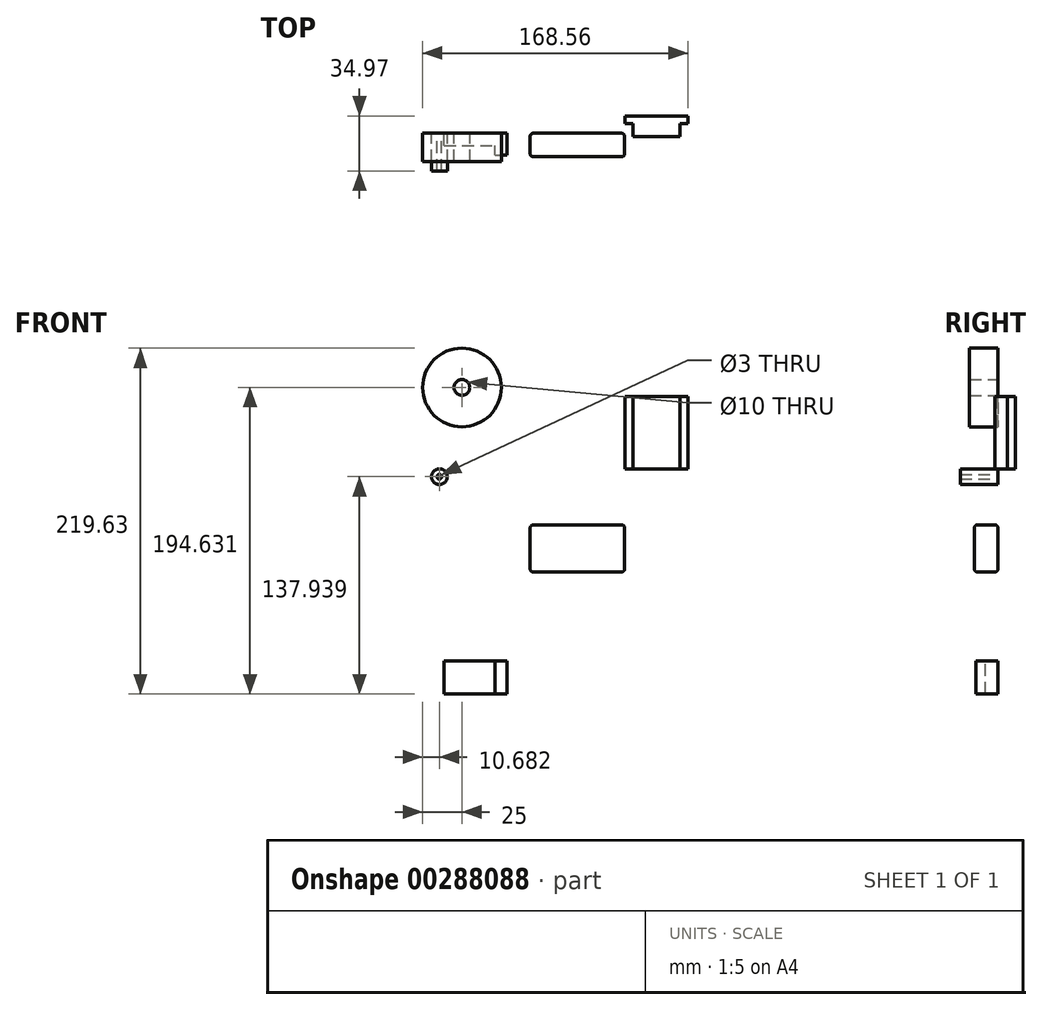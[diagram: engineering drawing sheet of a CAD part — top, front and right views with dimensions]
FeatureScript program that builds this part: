
annotation { "Feature Type Name" : "Feature", "Feature Type Description" : "" }
export const myFeature = defineFeature(function(context is Context, id is Id, definition is map)
    precondition{}
    {
        {
            var Q0;
            Q0=qCreatedBy(makeId("Front.planeOp"),FACE);
            var sketch = newSketch(context, id + "F0", { "sketchPlane" : qUnion([Q0])});
            skCircle(sketch, "E0", {"center": v(-49.92, 51.66) * mm, "radius": 25 * mm});
            skCircle(sketch, "E1", {"center": v(-49.92, 51.66) * mm, "radius": 5 * mm});
            skSolve(sketch);
        }
        {
            var Q0;
            Q0=makeQuery(id+"F0.imprint","IMPRINT",FACE,{"disambiguationData":[TD([[makeQuery(id+"F0.imprint","IMPRINT",EDGE,{"derivedFrom":sQuery(id+"F0.wireOp",EDGE,"E0")}),1.0]])]});
            extrude(context, id + "F1", {"entities" : qUnion([Q0]), "depth" : 18 * mm});
        }
        {
            var Q0;
            Q0=qCreatedBy(makeId("Front.planeOp"),FACE);
            var sketch = newSketch(context, id + "F2", { "sketchPlane" : qUnion([Q0])});
            skCircle(sketch, "E2", {"center": v(-64.24, -5.03) * mm, "radius": 5 * mm});
            skCircle(sketch, "E3", {"center": v(-64.24, -5.03) * mm, "radius": 1.5 * mm});
            skSolve(sketch);
        }
        {
            var Q0;
            Q0=qSketchRegion(id+"F2",true);
            extrude(context, id + "F3", {"entities" : qUnion([Q0]), "depth" : 24 * mm});
        }
        {
            var Q0;
            Q0=qCreatedBy(makeId("Front.planeOp"),FACE);
            var sketch = newSketch(context, id + "F4", { "sketchPlane" : qUnion([Q0])});
            skLineSegment(sketch, "E4.bottom", {"start": v(53.43, -35.58) * mm, "end": v(-6.57, -35.58) * mm});
            skLineSegment(sketch, "E4.top", {"start": v(53.43, -65.58) * mm, "end": v(-6.57, -65.58) * mm});
            skLineSegment(sketch, "E4.left", {"start": v(53.43, -35.58) * mm, "end": v(53.43, -65.58) * mm});
            skLineSegment(sketch, "E4.right", {"start": v(-6.57, -35.58) * mm, "end": v(-6.57, -65.58) * mm});
            skSolve(sketch);
        }
        {
            var Q0;
            Q0=qSketchRegion(id+"F4",true);
            extrude(context, id + "F5", {"entities" : qUnion([Q0]), "depth" : 15 * mm});
        }
        {
            var Q0;
            Q0=makeQuery(id+"F5.opExtrude","CAP_FACE",FACE,{"disambiguationData":[OSD([sQuery(id+"F4.wireOp",EDGE,"E4.bottom"),sQuery(id+"F4.wireOp",EDGE,"E4.top"),sQuery(id+"F4.wireOp",EDGE,"E4.left"),sQuery(id+"F4.wireOp",EDGE,"E4.right")])],"isStart":false});
            var Q1;
            Q1=makeQuery(id+"F5.opExtrude","CAP_FACE",FACE,{"disambiguationData":[OSD([sQuery(id+"F4.wireOp",EDGE,"E4.bottom"),sQuery(id+"F4.wireOp",EDGE,"E4.top"),sQuery(id+"F4.wireOp",EDGE,"E4.left"),sQuery(id+"F4.wireOp",EDGE,"E4.right")])],"isStart":true});
            var Q2;
            Q2=makeQuery(id+"F5.opExtrude","SWEPT_FACE",FACE,{"disambiguationData":[OSD([sQuery(id+"F4.wireOp",EDGE,"E4.top")])]});
            var Q3;
            Q3=makeQuery(id+"F5.opExtrude","SWEPT_FACE",FACE,{"disambiguationData":[OSD([sQuery(id+"F4.wireOp",EDGE,"E4.bottom")])]});
            fillet(context, id + "F6", {"entities" : qUnion([Q0, Q1, Q2, Q3]), "radius" : 2 * mm, "tangentPropagation" : true, "allowEdgeOverflow" : false});
        }
        {
            var Q0;
            Q0=qCreatedBy(makeId("Front.planeOp"),FACE);
            var sketch = newSketch(context, id + "F7", { "sketchPlane" : qUnion([Q0])});
            skLineSegment(sketch, "E5.bottom", {"start": v(-61.23, -121.97) * mm, "end": v(-21.23, -121.97) * mm});
            skLineSegment(sketch, "E5.top", {"start": v(-61.23, -142.97) * mm, "end": v(-21.23, -142.97) * mm});
            skLineSegment(sketch, "E5.left", {"start": v(-61.23, -121.97) * mm, "end": v(-61.23, -142.97) * mm});
            skLineSegment(sketch, "E5.right", {"start": v(-21.23, -121.97) * mm, "end": v(-21.23, -142.97) * mm});
            skSolve(sketch);
        }
        {
            var Q0;
            Q0=qSketchRegion(id+"F7",true);
            extrude(context, id + "F8", {"entities" : qUnion([Q0]), "depth" : 8 * mm});
        }
        {
            var Q0;
            Q0=makeQuery(id+"F8.opExtrude","CAP_FACE",FACE,{"disambiguationData":[OSD([sQuery(id+"F7.wireOp",EDGE,"E5.bottom"),sQuery(id+"F7.wireOp",EDGE,"E5.top"),sQuery(id+"F7.wireOp",EDGE,"E5.left"),sQuery(id+"F7.wireOp",EDGE,"E5.right")])],"isStart":false});
            var sketch = newSketch(context, id + "F9", { "sketchPlane" : qUnion([Q0])});
            skLineSegment(sketch, "E6.bottom", {"start": v(-21.23, -142.97) * mm, "end": v(-28.77, -142.97) * mm});
            skLineSegment(sketch, "E6.top", {"start": v(-21.23, -121.97) * mm, "end": v(-28.77, -121.97) * mm});
            skLineSegment(sketch, "E6.left", {"start": v(-21.23, -142.97) * mm, "end": v(-21.23, -121.97) * mm});
            skLineSegment(sketch, "E6.right", {"start": v(-28.77, -142.97) * mm, "end": v(-28.77, -121.97) * mm});
            skSolve(sketch);
        }
        {
            var Q0;
            Q0=qSketchRegion(id+"F9",true);
            extrude(context, id + "F10", {"entities" : qUnion([Q0]), "operationType" : NewBodyOperationType.ADD, "depth" : 6 * mm});
        }
        {
            var Q0;
            Q0=qCreatedBy(makeId("Top.planeOp"),FACE);
            var sketch = newSketch(context, id + "F11", { "sketchPlane" : qUnion([Q0])});
            skLineSegment(sketch, "E7", {"start": v(53.64, 10.97) * mm, "end": v(93.64, 10.97) * mm});
            skLineSegment(sketch, "E8", {"start": v(93.64, 10.97) * mm, "end": v(93.64, 5.97) * mm});
            skLineSegment(sketch, "E9", {"start": v(93.64, 5.97) * mm, "end": v(88.64, 5.97) * mm});
            skLineSegment(sketch, "E10", {"start": v(88.64, 5.97) * mm, "end": v(88.64, -2.03) * mm});
            skLineSegment(sketch, "E11", {"start": v(88.64, -2.03) * mm, "end": v(58.64, -2.03) * mm});
            skLineSegment(sketch, "E12", {"start": v(58.64, -2.03) * mm, "end": v(58.64, 5.97) * mm});
            skLineSegment(sketch, "E13", {"start": v(58.64, 5.97) * mm, "end": v(53.64, 5.97) * mm});
            skLineSegment(sketch, "E14", {"start": v(53.64, 5.97) * mm, "end": v(53.64, 10.97) * mm});
            skSolve(sketch);
        }
        {
            var Q0;
            Q0=qSketchRegion(id+"F11",true);
            extrude(context, id + "F12", {"entities" : qUnion([Q0]), "depth" : 46 * mm});
        }
    });
